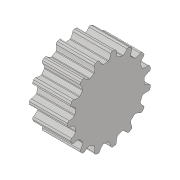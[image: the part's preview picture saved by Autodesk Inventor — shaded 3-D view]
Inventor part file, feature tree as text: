
AUTODESK INVENTOR PART (.ipt)
format: ipt  version: 2019.4 (Build 234330000, 330)  size: 219,648 bytes
history: native  units: mm
features: fillet x2, other x1, extrude x1, pattern_circular x1, sketch x1
ambient origin geometry x8: Origin, YZ Plane, XZ Plane, XY Plane, X Axis, Y Axis, Z Axis, Center Point
bodies: Body1 (feature_tree)
feature tree (6):
  other  "ソリッド1"
  extrude  "押し出し1"  Depth=1.95mm
  fillet  "フィレット1"  Radius=1.975mm
  fillet  "フィレット2"  Radius=1.11mm
  pattern_circular  "円形状パターン1"  [2 undecoded]
  sketch  "スケッチ1"
note: 2 required parameter values undecoded (feature->parameter linkage not recoverable at this tier; creation-order binding heuristic only, values carry confidence <= 0.55)
